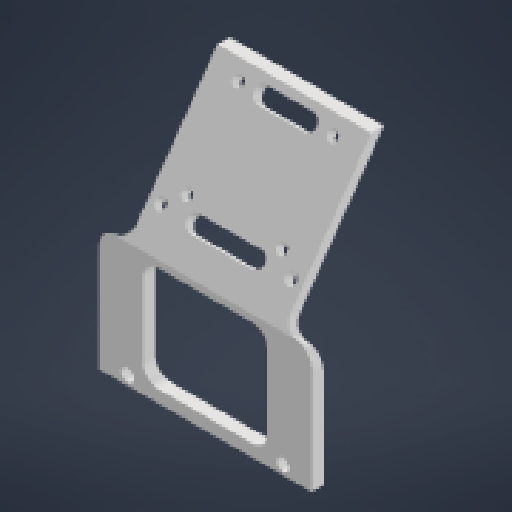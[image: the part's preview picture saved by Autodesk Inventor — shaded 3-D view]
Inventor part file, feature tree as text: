
AUTODESK INVENTOR PART (.ipt)
format: ipt  version: 2023 (Build 270158000, 158)  size: 260,608 bytes
history: native  units: in
note: dims shown in document units (in); Inventor stores cm internally (conversion verified against a paired STEP export)
features: sketch x9, extrude x6, reference x6, hole x3, fillet x3, projected_geometry x3, other x3
ambient origin geometry x8: Origin, YZ Plane, XZ Plane, XY Plane, X Axis, Y Axis, Z Axis, Center Point
bodies: Solid1 (feature_tree)
feature tree (33):
  extrude  "Extrusion1"  Depth=0.3779in
  extrude  "Extrusion2"  Depth=1.9685in
  hole  "Hole1"  [1 undecoded]
  extrude  "Extrusion3"  Depth=0.0787in
  extrude  "Extrusion4"  Depth=0.1969in
  hole  "Hole2"  [1 undecoded]
  extrude  "Extrusion5"  Depth=0.1969in
  fillet  "Fillet1"  Radius=0.1969in
  extrude  "Extrusion6"  Depth=0.1969in
  fillet  "Fillet2"  Radius=0.8268in
  hole  "Hole3"  [1 undecoded]
  fillet  "Fillet3"  [1 undecoded]
  sketch  "Sketch1"  dims[d0=0.1575in d1=0.0in d2=0.3779in]
  reference  "Reference1"
  sketch  "Sketch2"  dims[d3=0.1575in d4=0.0in d5=1.9685in]
  projected_geometry  "Projected Loop1"
  sketch  "Sketch4"  dims[d11=0.9185in d12=0.8831in]
  sketch  "Sketch5"  dims[d13=0.1969in]
  projected_geometry  "Projected Loop2"
  sketch  "Sketch6"  dims[d14=0.1378in d15=0.2362in d16=0.1575in d17=0.0787in d18=90.0deg d19=0.315in d20=0.8108in d25=0.9185in]
  sketch  "Sketch7"  dims[d26=0.1969in d27=0.4331in]
  sketch  "Sketch8"  dims[d28=0.4593in d29=0.0in d30=0.0in]
  reference  "Reference2"
  projected_geometry  "Projected Loop3"
  sketch  "Sketch9"  dims[d31=0.1969in d32=0.7874in d33=0.1969in]
  reference  "Reference3"
  reference  "Reference4"
  sketch  "Sketch10"  dims[d34=0.3937in d35=0.0in d36=1.6535in d37=0.8268in d38=0.1378in d39=0.2362in d40=0.1575in d41=0.0787in d42=90.0deg d43=0.315in d44=0.8108in d45=0.4528in d48=0.0in d49=0.0in d50=0.374in d51=0.374in d52=0.1575in d53=0.1969in d54=0.1575in d55=0.0in d56=0.0in d57=0.1969in d58=0.1575in d59=0.2362in d60=0.1575in d61=0.0787in d62=90.0deg d63=0.315in d64=0.8108in d65=0.1969in]
  reference  "Reference5"
  reference  "Reference6"
  other  "aim-a-lyzer assy.iam"
  other  "Discovery boar holder:1"
  other  "Discovery board:1"
note: 4 required parameter values undecoded (feature->parameter linkage not recoverable at this tier; creation-order binding heuristic only, values carry confidence <= 0.55)
